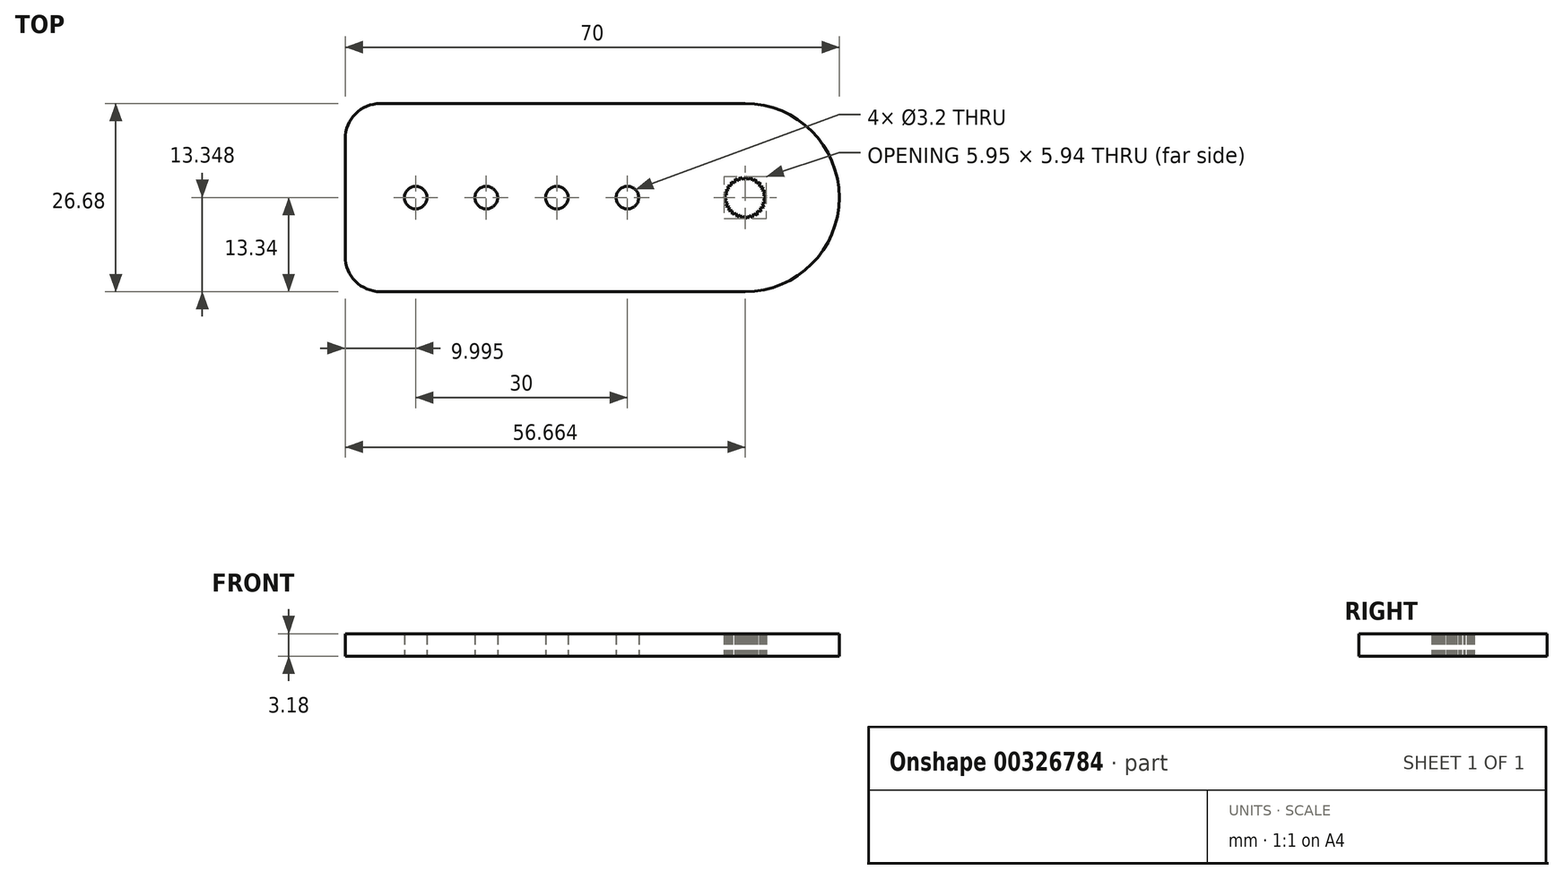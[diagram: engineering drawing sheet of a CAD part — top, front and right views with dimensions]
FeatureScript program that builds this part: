
annotation { "Feature Type Name" : "Feature", "Feature Type Description" : "" }
export const myFeature = defineFeature(function(context is Context, id is Id, definition is map)
    precondition{}
    {
        {
            var Q0;
            Q0=qCreatedBy(makeId("Top.planeOp"),FACE);
            var sketch = newSketch(context, id + "F0", { "sketchPlane" : qUnion([Q0])});
            skCircle(sketch, "E0", {"center": v(-46.66, 0) * mm, "radius": 1.6 * mm});
            skCircle(sketch, "E1.1.0.0", {"center": v(-36.66, 0) * mm, "radius": 1.6 * mm});
            skCircle(sketch, "E1.2.0.0", {"center": v(-26.66, 0) * mm, "radius": 1.6 * mm});
            skLineSegment(sketch, "E1.direction1", {"start": v(-46.66, 0) * mm, "end": v(-36.66, 0) * mm, "construction": true});
            skLineSegment(sketch, "E2.MirrorCS", {"start": v(0, 13.34) * mm, "end": v(0, 13.34) * mm});
            skLineSegment(sketch, "E3", {"start": v(-2.48, 1.65) * mm, "end": v(-2.31, 1.15) * mm});
            skLineSegment(sketch, "E4", {"start": v(-2.31, 1.15) * mm, "end": v(-2.81, 0.98) * mm});
            skLineSegment(sketch, "E5.1.0", {"start": v(-2.81, 0.98) * mm, "end": v(-2.53, 0.54) * mm});
            skLineSegment(sketch, "E5.1.1", {"start": v(-2.53, 0.54) * mm, "end": v(-2.97, 0.25) * mm});
            skLineSegment(sketch, "E5.2.0", {"start": v(-2.97, 0.25) * mm, "end": v(-2.58, -0.1) * mm});
            skLineSegment(sketch, "E5.2.1", {"start": v(-2.58, -0.1) * mm, "end": v(-2.94, -0.5) * mm});
            skLineSegment(sketch, "E5.3.0", {"start": v(-2.94, -0.5) * mm, "end": v(-2.47, -0.74) * mm});
            skLineSegment(sketch, "E5.3.1", {"start": v(-2.47, -0.74) * mm, "end": v(-2.72, -1.2) * mm});
            skLineSegment(sketch, "E5.4.0", {"start": v(-2.72, -1.2) * mm, "end": v(-2.21, -1.34) * mm});
            skLineSegment(sketch, "E5.4.1", {"start": v(-2.21, -1.34) * mm, "end": v(-2.34, -1.85) * mm});
            skLineSegment(sketch, "E5.5.0", {"start": v(-2.34, -1.85) * mm, "end": v(-1.8, -1.84) * mm});
            skLineSegment(sketch, "E5.5.1", {"start": v(-1.8, -1.84) * mm, "end": v(-1.8, -2.37) * mm});
            skLineSegment(sketch, "E5.6.0", {"start": v(-1.8, -2.37) * mm, "end": v(-1.3, -2.24) * mm});
            skLineSegment(sketch, "E5.6.1", {"start": v(-1.3, -2.24) * mm, "end": v(-1.16, -2.75) * mm});
            skLineSegment(sketch, "E5.7.0", {"start": v(-1.16, -2.75) * mm, "end": v(-0.7, -2.49) * mm});
            skLineSegment(sketch, "E5.7.1", {"start": v(-0.7, -2.49) * mm, "end": v(-0.44, -2.95) * mm});
            skLineSegment(sketch, "E5.8.0", {"start": v(-0.44, -2.95) * mm, "end": v(-0.06, -2.58) * mm});
            skLineSegment(sketch, "E5.8.1", {"start": v(-0.06, -2.58) * mm, "end": v(0.3, -2.96) * mm});
            skLineSegment(sketch, "E5.9.0", {"start": v(0.3, -2.96) * mm, "end": v(0.59, -2.52) * mm});
            skLineSegment(sketch, "E5.9.1", {"start": v(0.59, -2.52) * mm, "end": v(1.04, -2.8) * mm});
            skLineSegment(sketch, "E5.10.0", {"start": v(1.04, -2.8) * mm, "end": v(1.2, -2.3) * mm});
            skLineSegment(sketch, "E5.10.1", {"start": v(1.2, -2.3) * mm, "end": v(1.7, -2.45) * mm});
            skLineSegment(sketch, "E5.11.0", {"start": v(1.7, -2.45) * mm, "end": v(1.73, -1.92) * mm});
            skLineSegment(sketch, "E5.11.1", {"start": v(1.73, -1.92) * mm, "end": v(2.25, -1.95) * mm});
            skLineSegment(sketch, "E5.12.0", {"start": v(2.25, -1.95) * mm, "end": v(2.15, -1.43) * mm});
            skLineSegment(sketch, "E5.12.1", {"start": v(2.15, -1.43) * mm, "end": v(2.67, -1.33) * mm});
            skLineSegment(sketch, "E5.13.0", {"start": v(2.67, -1.33) * mm, "end": v(2.44, -0.85) * mm});
            skLineSegment(sketch, "E5.13.1", {"start": v(2.44, -0.85) * mm, "end": v(2.91, -0.62) * mm});
            skLineSegment(sketch, "E5.14.0", {"start": v(2.91, -0.62) * mm, "end": v(2.57, -0.22) * mm});
            skLineSegment(sketch, "E5.14.1", {"start": v(2.57, -0.22) * mm, "end": v(2.98, 0.12) * mm});
            skLineSegment(sketch, "E5.15.0", {"start": v(2.98, 0.12) * mm, "end": v(2.55, 0.43) * mm});
            skLineSegment(sketch, "E5.15.1", {"start": v(2.55, 0.43) * mm, "end": v(2.85, 0.86) * mm});
            skLineSegment(sketch, "E5.16.0", {"start": v(2.85, 0.86) * mm, "end": v(2.36, 1.05) * mm});
            skLineSegment(sketch, "E5.16.1", {"start": v(2.36, 1.05) * mm, "end": v(2.55, 1.54) * mm});
            skLineSegment(sketch, "E5.17.0", {"start": v(2.55, 1.54) * mm, "end": v(2.03, 1.6) * mm});
            skLineSegment(sketch, "E5.17.1", {"start": v(2.03, 1.6) * mm, "end": v(2.09, 2.13) * mm});
            skLineSegment(sketch, "E5.18.0", {"start": v(2.09, 2.13) * mm, "end": v(1.56, 2.06) * mm});
            skLineSegment(sketch, "E5.18.1", {"start": v(1.56, 2.06) * mm, "end": v(1.5, 2.58) * mm});
            skLineSegment(sketch, "E5.19.0", {"start": v(1.5, 2.58) * mm, "end": v(1, 2.38) * mm});
            skLineSegment(sketch, "E5.19.1", {"start": v(1, 2.38) * mm, "end": v(0.8, 2.87) * mm});
            skLineSegment(sketch, "E5.20.0", {"start": v(0.8, 2.87) * mm, "end": v(0.38, 2.56) * mm});
            skLineSegment(sketch, "E5.20.1", {"start": v(0.38, 2.56) * mm, "end": v(0.07, 2.98) * mm});
            skLineSegment(sketch, "E5.21.0", {"start": v(0.07, 2.98) * mm, "end": v(-0.27, 2.57) * mm});
            skLineSegment(sketch, "E5.21.1", {"start": v(-0.27, 2.57) * mm, "end": v(-0.68, 2.9) * mm});
            skLineSegment(sketch, "E5.22.0", {"start": v(-0.68, 2.9) * mm, "end": v(-0.9, 2.42) * mm});
            skLineSegment(sketch, "E5.22.1", {"start": v(-0.9, 2.42) * mm, "end": v(-1.38, 2.64) * mm});
            skLineSegment(sketch, "E5.23.0", {"start": v(-1.38, 2.64) * mm, "end": v(-1.47, 2.12) * mm});
            skLineSegment(sketch, "E5.23.1", {"start": v(-1.47, 2.12) * mm, "end": v(-2, 2.22) * mm});
            skLineSegment(sketch, "E5.24.0", {"start": v(-2, 2.22) * mm, "end": v(-1.95, 1.69) * mm});
            skLineSegment(sketch, "E5.24.1", {"start": v(-1.95, 1.69) * mm, "end": v(-2.48, 1.65) * mm});
            skPoint(sketch, "E5.center", {"position": v(0, 0) * mm});
            skPoint(sketch, "E6.orphan", {"position": v(0, 13.34) * mm});
            skPoint(sketch, "E7.orphan", {"position": v(0, 5) * mm});
            skPoint(sketch, "E8.orphan", {"position": v(0, -13.34) * mm});
            skLineSegment(sketch, "E9", {"start": v(7.5, 0) * mm, "end": v(7.5, 0) * mm});
            skPoint(sketch, "E10.MirrorCS.end.orphan", {"position": v(-37.6, 8.33) * mm});
            skPoint(sketch, "E10.MirrorCS.start.orphan", {"position": v(-32.6, 13.34) * mm});
            skPoint(sketch, "E11.MirrorCS.end.orphan", {"position": v(-37.6, -8.33) * mm});
            skPoint(sketch, "E11.MirrorCS.start.orphan", {"position": v(-32.6, -13.34) * mm});
            skArc(sketch, "E12.trimOffspring", {"start": v(0, -13.34) * mm, "mid": v(13.34, 0) * mm, "end": v(0, 13.34) * mm});
            skCircle(sketch, "E13.0.3.0", {"center": v(-16.66, 0) * mm, "radius": 1.6 * mm});
            skLineSegment(sketch, "E14.bottom", {"start": v(0, 13.34) * mm, "end": v(-51.66, 13.34) * mm});
            skLineSegment(sketch, "E14.top", {"start": v(0, -13.34) * mm, "end": v(-51.66, -13.34) * mm});
            skLineSegment(sketch, "E14.right", {"start": v(-56.66, 8.34) * mm, "end": v(-56.66, -8.34) * mm});
            skArc(sketch, "E15", {"start": v(-51.66, 13.34) * mm, "mid": v(-55.2, 11.87) * mm, "end": v(-56.66, 8.34) * mm});
            skArc(sketch, "E16", {"start": v(-56.66, -8.34) * mm, "mid": v(-55.2, -11.87) * mm, "end": v(-51.66, -13.34) * mm});
            skPoint(sketch, "E17.orphan", {"position": v(-56.66, -13.34) * mm});
            skSolve(sketch);
        }
        {
            var Q0;
            Q0=makeQuery(id+"F0.imprint","IMPRINT",FACE,{"disambiguationData":[TD([[makeQuery(id+"F0.imprint","IMPRINT",EDGE,{"derivedFrom":sQuery(id+"F0.wireOp",EDGE,"E1.2.0.0")}),-1.0]])]});
            extrude(context, id + "F1", {"entities" : qUnion([Q0]), "depth" : 3.17 * mm});
        }
    });
